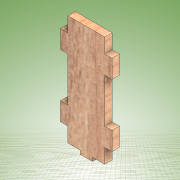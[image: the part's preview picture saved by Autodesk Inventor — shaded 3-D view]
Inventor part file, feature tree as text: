
AUTODESK INVENTOR PART (.ipt)
format: ipt  version: 2022 (Build 260153000, 153)  size: 169,984 bytes
history: native  units: mm
features: extrude x2, sketch x2, other x1
ambient origin geometry x8: Origin, YZ Plane, XZ Plane, XY Plane, X Axis, Y Axis, Z Axis, Center Point
bodies: Body1 (feature_tree)
feature tree (5):
  other  "Sólido1"
  extrude  "Extrusión1"  Depth=90.0mm
  extrude  "Extrusión3"  Depth=15.0mm
  sketch  "Boceto1"  dims[d0=30.0mm d1=90.0mm]
  sketch  "Boceto3"  dims[d2=6.0mm d3=15.0mm d4=12.0mm d5=6.0mm d6=0.0mm d11=10.0mm d12=3.0mm d13=0.0mm]
